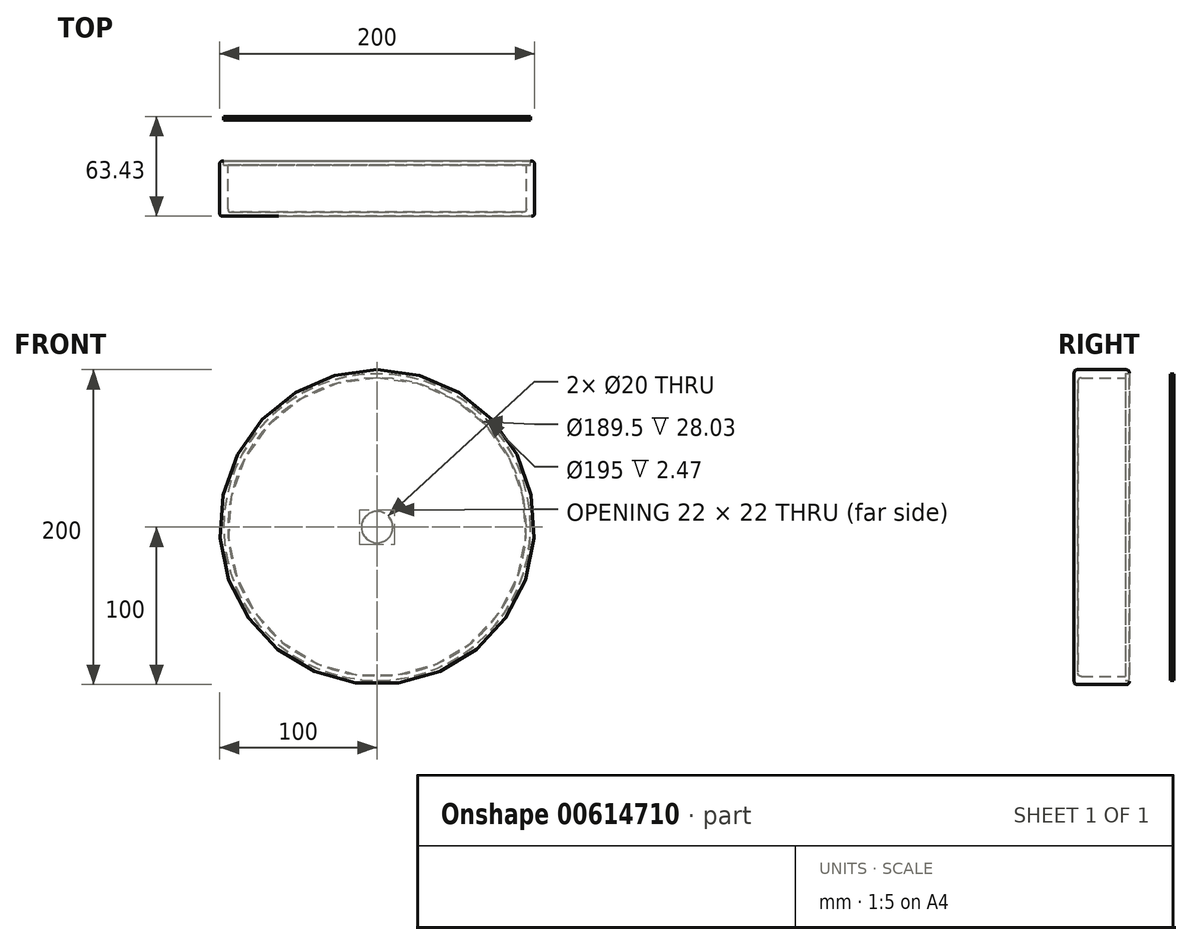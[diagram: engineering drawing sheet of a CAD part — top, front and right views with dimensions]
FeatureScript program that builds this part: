
annotation { "Feature Type Name" : "Feature", "Feature Type Description" : "" }
export const myFeature = defineFeature(function(context is Context, id is Id, definition is map)
    precondition{}
    {
        {
            var Q0;
            Q0=qCreatedBy(makeId("Top.planeOp"),FACE);
            var sketch = newSketch(context, id + "F0", { "sketchPlane" : qUnion([Q0])});
            skLineSegment(sketch, "E0", {"start": v(0, 0) * mm, "end": v(-100, 0) * mm});
            skLineSegment(sketch, "E1", {"start": v(-100, 0) * mm, "end": v(-100, 35) * mm});
            skLineSegment(sketch, "E2", {"start": v(-100, 35) * mm, "end": v(-97.5, 35) * mm});
            skLineSegment(sketch, "E3", {"start": v(-97.5, 35) * mm, "end": v(-97.5, 32.53) * mm});
            skLineSegment(sketch, "E4", {"start": v(-97.5, 32.53) * mm, "end": v(-94.75, 32.53) * mm});
            skLineSegment(sketch, "E5", {"start": v(-94.75, 32.53) * mm, "end": v(-94.75, 2.5) * mm});
            skLineSegment(sketch, "E6", {"start": v(-94.75, 2.5) * mm, "end": v(0, 2.5) * mm});
            skLineSegment(sketch, "E7", {"start": v(0, 38.69) * mm, "end": v(0, -31.42) * mm, "construction": true});
            skLineSegment(sketch, "E8.bottom", {"start": v(-97.4, 63.43) * mm, "end": v(-10, 63.43) * mm});
            skLineSegment(sketch, "E8.top", {"start": v(-97.4, 60.97) * mm, "end": v(-10, 60.97) * mm});
            skLineSegment(sketch, "E8.left", {"start": v(-97.4, 63.43) * mm, "end": v(-97.4, 60.97) * mm});
            skLineSegment(sketch, "E8.right", {"start": v(-10, 63.43) * mm, "end": v(-10, 60.97) * mm});
            skLineSegment(sketch, "E9", {"start": v(0, 2.5) * mm, "end": v(0, 0) * mm});
            skSolve(sketch);
        }
        {
            var Q0;
            Q0 = qSketchRegion(id + "F0", true);
            var Q1;
            Q1=sQuery(id+"F0.wireOp",EDGE,"E7");
            revolve(context, id + "F1", {"entities" : qUnion([Q0]), "axis" : qUnion([Q1]), "revolveType" : RevolveType.FULL, "surfaceOperationType" : NewSurfaceOperationType.NEW});
        }
        {
            var Q0;
            Q0=makeQuery(id+"F1.opRevolve","SWEPT_EDGE",EDGE,{"disambiguationData":[OSD([sQuery(id+"F0.wireOp",EDGE,"E5"),sQuery(id+"F0.wireOp",EDGE,"E6")])]});
            fillet(context, id + "F2", {"entities" : qUnion([Q0]), "radius" : 2 * mm, "rho" : 0.5, "crossSection" : FilletCrossSection.CONIC, "allowEdgeOverflow" : false});
        }
        {
            var Q0;
            Q0=makeQuery(id+"F1.opRevolve","SWEPT_EDGE",EDGE,{"disambiguationData":[OSD([sQuery(id+"F0.wireOp",EDGE,"E0"),sQuery(id+"F0.wireOp",EDGE,"E1")])]});
            fillet(context, id + "F3", {"entities" : qUnion([Q0]), "radius" : 2 * mm, "rho" : 0.5, "crossSection" : FilletCrossSection.CONIC, "allowEdgeOverflow" : false});
        }
        {
            var Q0;
            Q0=makeQuery(id+"F1.opRevolve","SWEPT_EDGE",EDGE,{"disambiguationData":[OSD([sQuery(id+"F0.wireOp",EDGE,"E1"),sQuery(id+"F0.wireOp",EDGE,"E2")])]});
            fillet(context, id + "F4", {"entities" : qUnion([Q0]), "radius" : 2 * mm, "rho" : 0.5, "crossSection" : FilletCrossSection.CONIC, "allowEdgeOverflow" : false});
        }
        {
            var Q0;
            Q0=makeQuery(id+"F0.imprint","IMPRINT",FACE,{"disambiguationData":[TD([[makeQuery(id+"F0.imprint","IMPRINT",EDGE,{"derivedFrom":sQuery(id+"F0.wireOp",EDGE,"E8.bottom")}),-1.0]])]});
            var Q1;
            Q1=sQuery(id+"F0.wireOp",EDGE,"E7");
            revolve(context, id + "F5", {"entities" : qUnion([Q0]), "axis" : qUnion([Q1]), "revolveType" : RevolveType.FULL, "surfaceOperationType" : NewSurfaceOperationType.NEW});
        }
        {
            var Q0;
            Q0=makeQuery(id+"F5.opRevolve","SWEPT_EDGE",EDGE,{"disambiguationData":[OSD([sQuery(id+"F0.wireOp",EDGE,"E8.top"),sQuery(id+"F0.wireOp",EDGE,"E8.right")])]});
            var Q1;
            Q1=makeQuery(id+"F5.opRevolve","SWEPT_EDGE",EDGE,{"disambiguationData":[OSD([sQuery(id+"F0.wireOp",EDGE,"E8.bottom"),sQuery(id+"F0.wireOp",EDGE,"E8.right")])]});
            fillet(context, id + "F6", {"entities" : qUnion([Q0, Q1]), "radius" : 1 * mm, "rho" : 0.5, "crossSection" : FilletCrossSection.CONIC, "allowEdgeOverflow" : false});
        }
    });
